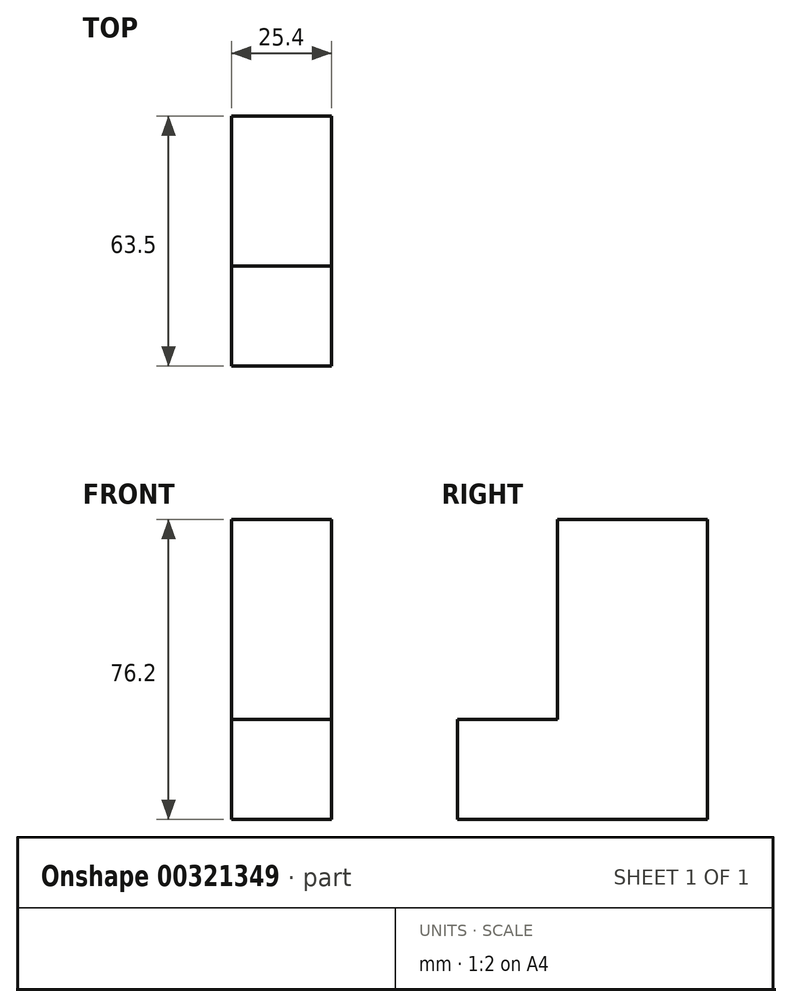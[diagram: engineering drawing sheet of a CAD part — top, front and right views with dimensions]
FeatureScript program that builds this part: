
annotation { "Feature Type Name" : "Feature", "Feature Type Description" : "" }
export const myFeature = defineFeature(function(context is Context, id is Id, definition is map)
    precondition{}
    {
        {
            var Q0;
            Q0=qCreatedBy(makeId("Right.planeOp"),FACE);
            var sketch = newSketch(context, id + "F0", { "sketchPlane" : qUnion([Q0])});
            skLineSegment(sketch, "E0", {"start": v(35.54, 39.73) * mm, "end": v(35.54, -36.47) * mm});
            skLineSegment(sketch, "E1", {"start": v(35.54, -36.47) * mm, "end": v(-27.96, -36.47) * mm});
            skLineSegment(sketch, "E2", {"start": v(-27.96, -36.47) * mm, "end": v(-27.96, -11.07) * mm});
            skLineSegment(sketch, "E3", {"start": v(-27.96, -11.07) * mm, "end": v(-2.56, -11.07) * mm});
            skLineSegment(sketch, "E4", {"start": v(-2.56, -11.07) * mm, "end": v(-2.56, 39.73) * mm});
            skLineSegment(sketch, "E5", {"start": v(-2.56, 39.73) * mm, "end": v(35.54, 39.73) * mm});
            skSolve(sketch);
        }
        {
            var Q0;
            Q0 = qSketchRegion(id + "F0", true);
            extrude(context, id + "F1", {"entities" : qUnion([Q0]), "depth" : 25.4 * mm});
        }
    });
